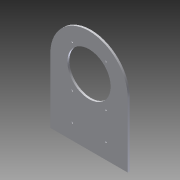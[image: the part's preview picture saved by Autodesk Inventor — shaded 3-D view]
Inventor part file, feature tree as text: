
AUTODESK INVENTOR PART (.ipt)
format: ipt  version: 2011 SP1 (Build 150282100, 282)  size: 98,816 bytes
history: native  units: in
note: dims shown in document units (in); Inventor stores cm internally (conversion verified against a paired STEP export)
features: hole x7, extrude x1, sketch x1
ambient origin geometry x8: Origin, YZ Plane, XZ Plane, XY Plane, X Axis, Y Axis, Z Axis, Center Point
bodies: Solid1 (feature_tree)
feature tree (9):
  extrude  "Extrusion1"  Depth=15.0in
  hole  "Hole1"  [1 undecoded]
  hole  "Hole2"  [1 undecoded]
  hole  "Hole3"  [1 undecoded]
  hole  "Hole4"  [1 undecoded]
  hole  "Hole5"  [1 undecoded]
  hole  "Hole6"  [1 undecoded]
  hole  "Hole7"  [1 undecoded]
  sketch  "Sketch1"  dims[d0=20.0in d1=15.0in d5=0.375in d6=0.0in d7=3.0in d8=4.25in d9=0.3125in d10=0.75in d11=0.375in d12=0.25in d13=0.5635in d14=1.0in d15=0.8108in d16=3.0in d17=4.25in d18=0.3125in d19=0.75in d20=0.375in d21=0.25in d22=0.5635in d23=1.0in d24=0.8108in d25=8.375in d26=4.25in d27=0.3125in d28=0.75in d29=0.375in d30=0.25in d31=0.5635in d32=1.0in d33=0.8108in d34=8.375in d35=4.25in d36=0.3125in d37=0.75in d38=0.375in d39=0.25in d40=0.5635in d41=1.0in d42=0.8108in d43=16.5in d44=4.25in d45=0.3125in d46=0.75in d47=0.375in d48=0.25in d49=0.5635in d50=1.0in d51=0.8108in d52=16.5in d53=4.25in d54=0.3125in d55=0.75in d56=0.375in d57=0.25in d58=0.5635in d59=1.0in d60=0.8108in d61=12.75in d62=7.5in d63=8.375in d64=0.75in d65=0.375in d66=0.25in d67=0.5635in d68=1.0in d69=0.8108in]
note: 7 required parameter values undecoded (feature->parameter linkage not recoverable at this tier; creation-order binding heuristic only, values carry confidence <= 0.55)
